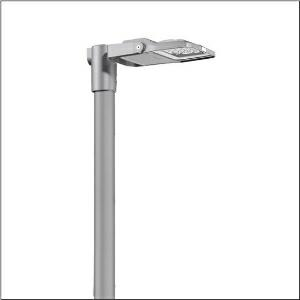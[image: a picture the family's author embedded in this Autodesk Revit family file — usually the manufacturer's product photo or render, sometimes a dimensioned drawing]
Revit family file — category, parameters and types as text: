
# Revit family: floodlight_fl_21_micro___pl43_5xa7762a2a3a_f020
name_source: partatom
category: Lighting Fixtures
units: mm (PartAtom-declared; Revit-internal decimal feet)

## family parameters
Cut with Voids When Loaded = No
Host = Face
Light Source = No
Part Type = Normal
Room Calculation Point = No
Round Connector Dimension = Use Diameter
Shared = No

## types (1)
- --- (1 x LED, 3040 lm, 23.1 W, 3000K)
    Apparent Load = 23 VA
    CIE Flux Codes = 29 80 99 100 100
    Color Rendering = 70
    Color Temperature = 3000K
    Default Elevation = 1800 mm
    Description = Floodlight FL 21 micro, floodlight, primary light control with lens, of PMMA, primary optical cover: protective disc, of toughened safety glass, transparent, light distribution: PL43, light emission: direct distribution, installation type: surface-mounted, LED, High Power LED, rated luminous flux: 3.040lm, luminous efficacy: 132lm/W, light colour: 730, colour temperature: 3000K, control gear: ECG iQ, control: Auto-Match, Temp-Guard, Night-Set, Smart-Wire, Desk-Remote (wireless, voltage-free reading and setting of iQ features in the workshop via application-optimized NFC function/RFID function), optimised constant luminous flux control (CLO 2.0), Street-Remote, with terminal, 6-pole, mains connection: 220..240V, AC, 50/60Hz, start of lifetime: 23W, end of lifetime: 24W, reduction: 11W, luminaire housing, of diecast aluminium, powder-coated, Siteco® metallic grey (DB 702S), corrosivity category C5 according to DIN EN ISO 12944, mast bracket, of steel, galvanised, powder-coated, Siteco® metallic grey (DB 702S), protection rating (complete): IP66, insulation class (complete): insulation class II (safety insulation), certification: CE, protection symbol: D, impact resistance: IK07, permissible operating ambient temperature: -40..+40°C, permissible operating ambient temperature for outdoor applications: -40..+50°C, standard: DIN EN 12944, packaging unit: 1 piece

Light Distribution: PL43
    Height = 65 mm
    Lamp = 1 x LED
    Lamp Light Flux = 3040 lm
    Lamp Power = 23.1 W
    Lamp count = 1
    Length = 312 mm
    Luminous efficacy = 132 lm/W
    Manufacturer = Siteco
    ModVariant = No
    Model = 5XA7762A2A3A
    Number of Poles = 1
    OnlyDefault = Yes
    Power Factor = 1
    Product Name = Floodlight FL 21 micro | PL43
    Product group = floodlight | pylon top
    ProductGroupID = 6101
    Protection Class = Protection class II
    Protection Degree = IP 66
    RLX_Detail_Level = 1
    RlxData = <blob elided: 101493 chars, md5=b4885b2d>
    Socket = socket
    Standby Power = 0 W
    System Light Flux = 3040 lm
    System Power = 23 W
    Type Comments = factory setting: luminous flux: 100 % | dim-lin: 254 | 455 mA
    Type Image = l_1007121.jpg
    URL = http://relux.com
    VarID = @adj_089857
    Voltage = 0 V
    Weight = 0.00 kg
    Width = 230 mm

## geometry (parser evidence)
native form markers: Blend x4, Sweep x13
no freeform markers — native parametric forms only
